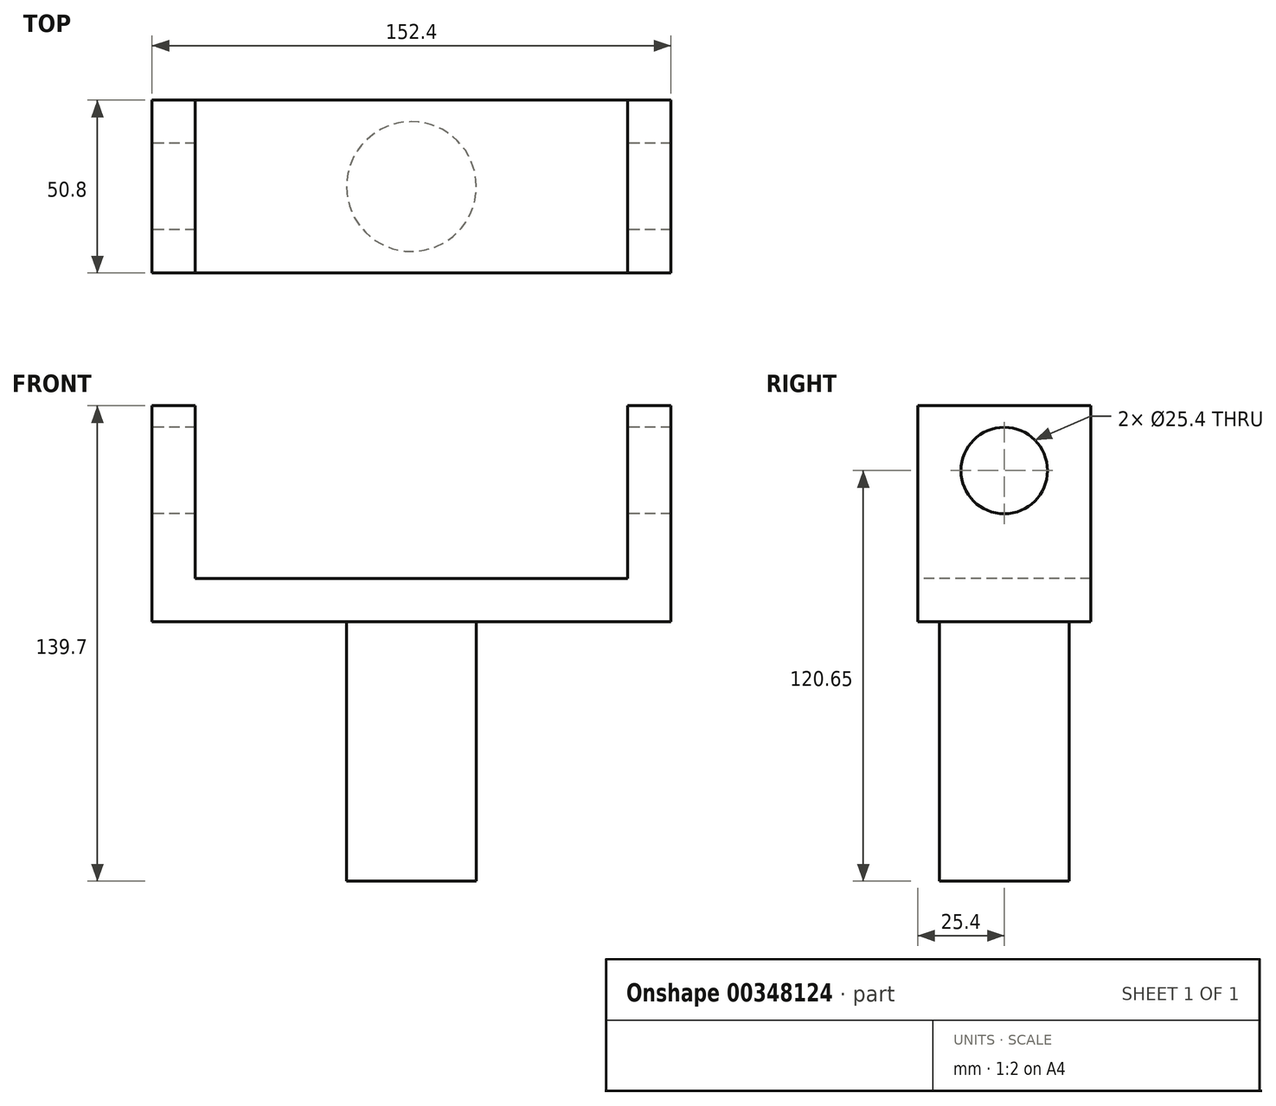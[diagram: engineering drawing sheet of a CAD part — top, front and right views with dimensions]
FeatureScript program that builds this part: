
annotation { "Feature Type Name" : "Feature", "Feature Type Description" : "" }
export const myFeature = defineFeature(function(context is Context, id is Id, definition is map)
    precondition{}
    {
        {
            var Q0;
            Q0=qCreatedBy(makeId("Top.planeOp"),FACE);
            var sketch = newSketch(context, id + "F0", { "sketchPlane" : qUnion([Q0])});
            skCircle(sketch, "E0", {"center": v(0, 0) * mm, "radius": 19.05 * mm});
            skSolve(sketch);
        }
        {
            var Q0;
            Q0=makeQuery(id+"F0.imprint","IMPRINT",FACE,{"disambiguationData":[TD([[makeQuery(id+"F0.imprint","IMPRINT",EDGE,{"derivedFrom":sQuery(id+"F0.wireOp",EDGE,"E0")}),1.0]])]});
            extrude(context, id + "F1", {"entities" : qUnion([Q0]), "depth" : 76.2 * mm});
        }
        {
            var Q0;
            Q0=makeQuery(id+"F1.opExtrude","CAP_FACE",FACE,{"disambiguationData":[OSD([sQuery(id+"F0.wireOp",EDGE,"E0")])],"isStart":false});
            var sketch = newSketch(context, id + "F2", { "sketchPlane" : qUnion([Q0])});
            skLineSegment(sketch, "E1.bottom", {"start": v(-76.2, 25.4) * mm, "end": v(76.2, 25.4) * mm});
            skLineSegment(sketch, "E1.top", {"start": v(-76.2, -25.4) * mm, "end": v(76.2, -25.4) * mm});
            skLineSegment(sketch, "E1.left", {"start": v(-76.2, 25.4) * mm, "end": v(-76.2, -25.4) * mm});
            skLineSegment(sketch, "E1.right", {"start": v(76.2, 25.4) * mm, "end": v(76.2, -25.4) * mm});
            skSolve(sketch);
        }
        {
            var Q0;
            Q0=makeQuery(id+"F2.imprint","IMPRINT",FACE,{"disambiguationData":[TD([[makeQuery(id+"F2.imprint","IMPRINT",EDGE,{"derivedFrom":sQuery(id+"F2.wireOp",EDGE,"E1.bottom")}),-1.0]])]});
            var Q1;
            Q1=makeQuery(id+"F2.imprint","IMPRINT",FACE,{"disambiguationData":[TD([[makeQuery(id+"F2.imprint","IMPRINT",EDGE,{"derivedFrom":makeQuery(id+"F1.opExtrude","CAP_EDGE",EDGE,{"disambiguationData":[OSD([sQuery(id+"F0.wireOp",EDGE,"E0")])],"isStart":false})}),1.0]])]});
            extrude(context, id + "F3", {"entities" : qUnion([Q0, Q1]), "operationType" : NewBodyOperationType.ADD, "depth" : 12.7 * mm});
        }
        {
            var Q0;
            Q0=makeQuery(id+"F3.opExtrude","CAP_FACE",FACE,{"disambiguationData":[OSD([sQuery(id+"F2.wireOp",EDGE,"E1.bottom"),sQuery(id+"F2.wireOp",EDGE,"E1.top"),sQuery(id+"F2.wireOp",EDGE,"E1.left"),sQuery(id+"F2.wireOp",EDGE,"E1.right")])],"isStart":false});
            var sketch = newSketch(context, id + "F4", { "sketchPlane" : qUnion([Q0])});
            skLineSegment(sketch, "E2.bottom", {"start": v(-76.2, 25.4) * mm, "end": v(-63.5, 25.4) * mm});
            skLineSegment(sketch, "E2.top", {"start": v(-76.2, -25.4) * mm, "end": v(-63.5, -25.4) * mm});
            skLineSegment(sketch, "E2.left", {"start": v(-76.2, 25.4) * mm, "end": v(-76.2, -25.4) * mm});
            skLineSegment(sketch, "E2.right", {"start": v(-63.5, 25.4) * mm, "end": v(-63.5, -25.4) * mm});
            skLineSegment(sketch, "E3.bottom", {"start": v(76.2, 25.4) * mm, "end": v(63.5, 25.4) * mm});
            skLineSegment(sketch, "E3.top", {"start": v(76.2, -25.4) * mm, "end": v(63.5, -25.4) * mm});
            skLineSegment(sketch, "E3.left", {"start": v(76.2, 25.4) * mm, "end": v(76.2, -25.4) * mm});
            skLineSegment(sketch, "E3.right", {"start": v(63.5, 25.4) * mm, "end": v(63.5, -25.4) * mm});
            skSolve(sketch);
        }
        {
            var Q0;
            Q0=makeQuery(id+"F4.imprint","IMPRINT",FACE,{"disambiguationData":[TD([[makeQuery(id+"F4.imprint","IMPRINT",EDGE,{"derivedFrom":sQuery(id+"F4.wireOp",EDGE,"E2.bottom")}),-1.0]])]});
            var Q1;
            Q1=makeQuery(id+"F4.imprint","IMPRINT",FACE,{"disambiguationData":[TD([[makeQuery(id+"F4.imprint","IMPRINT",EDGE,{"derivedFrom":sQuery(id+"F4.wireOp",EDGE,"E3.bottom")}),-1.0]])]});
            extrude(context, id + "F5", {"entities" : qUnion([Q0, Q1]), "operationType" : NewBodyOperationType.ADD, "depth" : 50.8 * mm});
        }
        {
            var Q0;
            Q0=makeQuery(id+"F5.boolean.opBoolean","MERGE",FACE,{"derivedFrom":[makeQuery(id+"F3.opExtrude","SWEPT_FACE",FACE,{"disambiguationData":[OSD([sQuery(id+"F2.wireOp",EDGE,"E1.left")])]}),makeQuery(id+"F5.opExtrude","SWEPT_FACE",FACE,{"disambiguationData":[OSD([sQuery(id+"F4.wireOp",EDGE,"E2.left")])]})]});
            var sketch = newSketch(context, id + "F6", { "sketchPlane" : qUnion([Q0])});
            skCircle(sketch, "E4", {"center": v(0, 120.65) * mm, "radius": 12.7 * mm});
            skSolve(sketch);
        }
        {
            var Q0;
            Q0=makeQuery(id+"F6.imprint","IMPRINT",FACE,{"disambiguationData":[TD([[makeQuery(id+"F6.imprint","IMPRINT",EDGE,{"derivedFrom":sQuery(id+"F6.wireOp",EDGE,"E4")}),1.0]])]});
            extrude(context, id + "F7", {"entities" : qUnion([Q0]), "operationType" : NewBodyOperationType.REMOVE, "oppositeDirection" : true, "depth" : 304.8 * mm});
        }
    });
